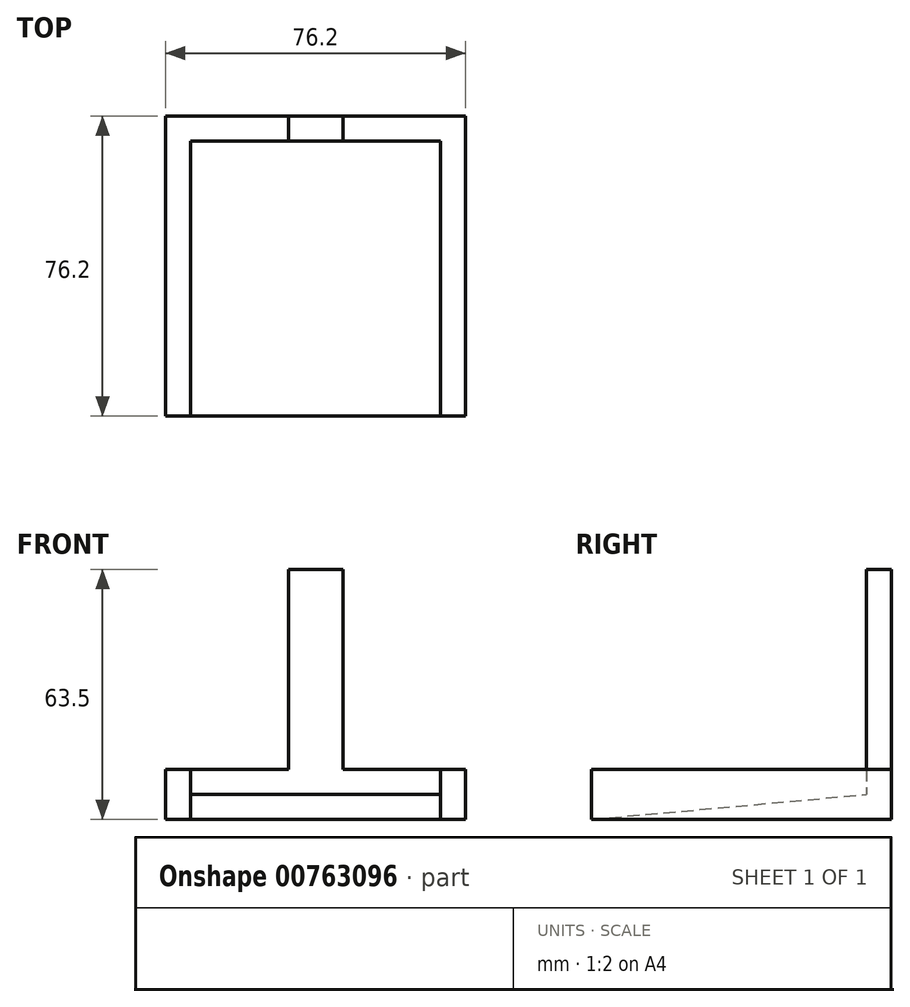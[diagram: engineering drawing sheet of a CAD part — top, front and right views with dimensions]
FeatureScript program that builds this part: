
annotation { "Feature Type Name" : "Feature", "Feature Type Description" : "" }
export const myFeature = defineFeature(function(context is Context, id is Id, definition is map)
    precondition{}
    {
        {
            var Q0;
            Q0=qCreatedBy(makeId("Top.planeOp"),FACE);
            var sketch = newSketch(context, id + "F0", { "sketchPlane" : qUnion([Q0])});
            skLineSegment(sketch, "E0.bottom", {"start": v(0, 0) * mm, "end": v(-76.2, 0) * mm});
            skLineSegment(sketch, "E0.top", {"start": v(0, -76.2) * mm, "end": v(-76.2, -76.2) * mm});
            skLineSegment(sketch, "E0.left", {"start": v(0, 0) * mm, "end": v(0, -76.2) * mm});
            skLineSegment(sketch, "E0.right", {"start": v(-76.2, 0) * mm, "end": v(-76.2, -76.2) * mm});
            skLineSegment(sketch, "E1", {"start": v(-38.1, -6.35) * mm, "end": v(-2.71, -6.35) * mm});
            skLineSegment(sketch, "E2", {"start": v(-6.35, -38.1) * mm, "end": v(-6.35, -6.35) * mm});
            skLineSegment(sketch, "E3.bottom", {"start": v(-6.35, -6.35) * mm, "end": v(-69.85, -6.35) * mm});
            skLineSegment(sketch, "E3.top", {"start": v(-6.35, -76.2) * mm, "end": v(-69.85, -76.2) * mm});
            skLineSegment(sketch, "E3.left", {"start": v(-6.35, -6.35) * mm, "end": v(-6.35, -76.2) * mm});
            skLineSegment(sketch, "E3.right", {"start": v(-69.85, -6.35) * mm, "end": v(-69.85, -76.2) * mm});
            skSolve(sketch);
        }
        {
            var Q0;
            Q0=makeQuery(id+"F0.imprint","IMPRINT",FACE,{"disambiguationData":[TD([[makeQuery(id+"F0.imprint","IMPRINT",EDGE,{"derivedFrom":sQuery(id+"F0.wireOp",EDGE,"E0.bottom")}),1.0]])]});
            extrude(context, id + "F1", {"entities" : qUnion([Q0]), "depth" : 12.7 * mm, "offsetDistance" : 25.4 * mm});
        }
        {
            var Q0;
            Q0=makeQuery(id+"F1.opExtrude","SWEPT_FACE",FACE,{"disambiguationData":[OSD([sQuery(id+"F0.wireOp",EDGE,"E3.right")])]});
            var sketch = newSketch(context, id + "F2", { "sketchPlane" : qUnion([Q0])});
            skLineSegment(sketch, "E4", {"start": v(-6.35, 0) * mm, "end": v(-76.2, 0) * mm});
            skLineSegment(sketch, "E5", {"start": v(-76.2, 0) * mm, "end": v(-6.35, 6.35) * mm});
            skLineSegment(sketch, "E6", {"start": v(-6.35, 6.35) * mm, "end": v(-6.35, 0) * mm});
            skSolve(sketch);
        }
        {
            var Q0;
            Q0 = qSketchRegion(id + "F2", true);
            extrude(context, id + "F3", {"entities" : qUnion([Q0]), "operationType" : NewBodyOperationType.ADD, "depth" : 63.5 * mm, "offsetDistance" : 25.4 * mm});
        }
        {
            var Q0;
            Q0=makeQuery(id+"F1.opExtrude","CAP_FACE",FACE,{"disambiguationData":[OSD([sQuery(id+"F0.wireOp",EDGE,"E0.bottom"),sQuery(id+"F0.wireOp",EDGE,"E0.top"),sQuery(id+"F0.wireOp",EDGE,"E0.left"),sQuery(id+"F0.wireOp",EDGE,"E0.right"),sQuery(id+"F0.wireOp",EDGE,"E3.bottom"),sQuery(id+"F0.wireOp",EDGE,"E3.left"),sQuery(id+"F0.wireOp",EDGE,"E3.right")])],"isStart":false});
            var sketch = newSketch(context, id + "F4", { "sketchPlane" : qUnion([Q0])});
            skLineSegment(sketch, "E7.bottom", {"start": v(-31.18, -6.35) * mm, "end": v(-45.02, -6.35) * mm});
            skPoint(sketch, "E7.middle", {"position": v(-38.1, 0) * mm});
            skLineSegment(sketch, "E8.bottom", {"start": v(-45.02, 0) * mm, "end": v(-31.18, 0) * mm});
            skLineSegment(sketch, "E8.top", {"start": v(-45.02, -6.35) * mm, "end": v(-31.18, -6.35) * mm});
            skLineSegment(sketch, "E8.left", {"start": v(-45.02, 0) * mm, "end": v(-45.02, -6.35) * mm});
            skLineSegment(sketch, "E8.right", {"start": v(-31.18, 0) * mm, "end": v(-31.18, -6.35) * mm});
            skSolve(sketch);
        }
        {
            var Q0;
            Q0 = qSketchRegion(id + "F4", true);
            extrude(context, id + "F5", {"entities" : qUnion([Q0]), "operationType" : NewBodyOperationType.ADD, "depth" : 50.8 * mm, "offsetDistance" : 25.4 * mm});
        }
    });
